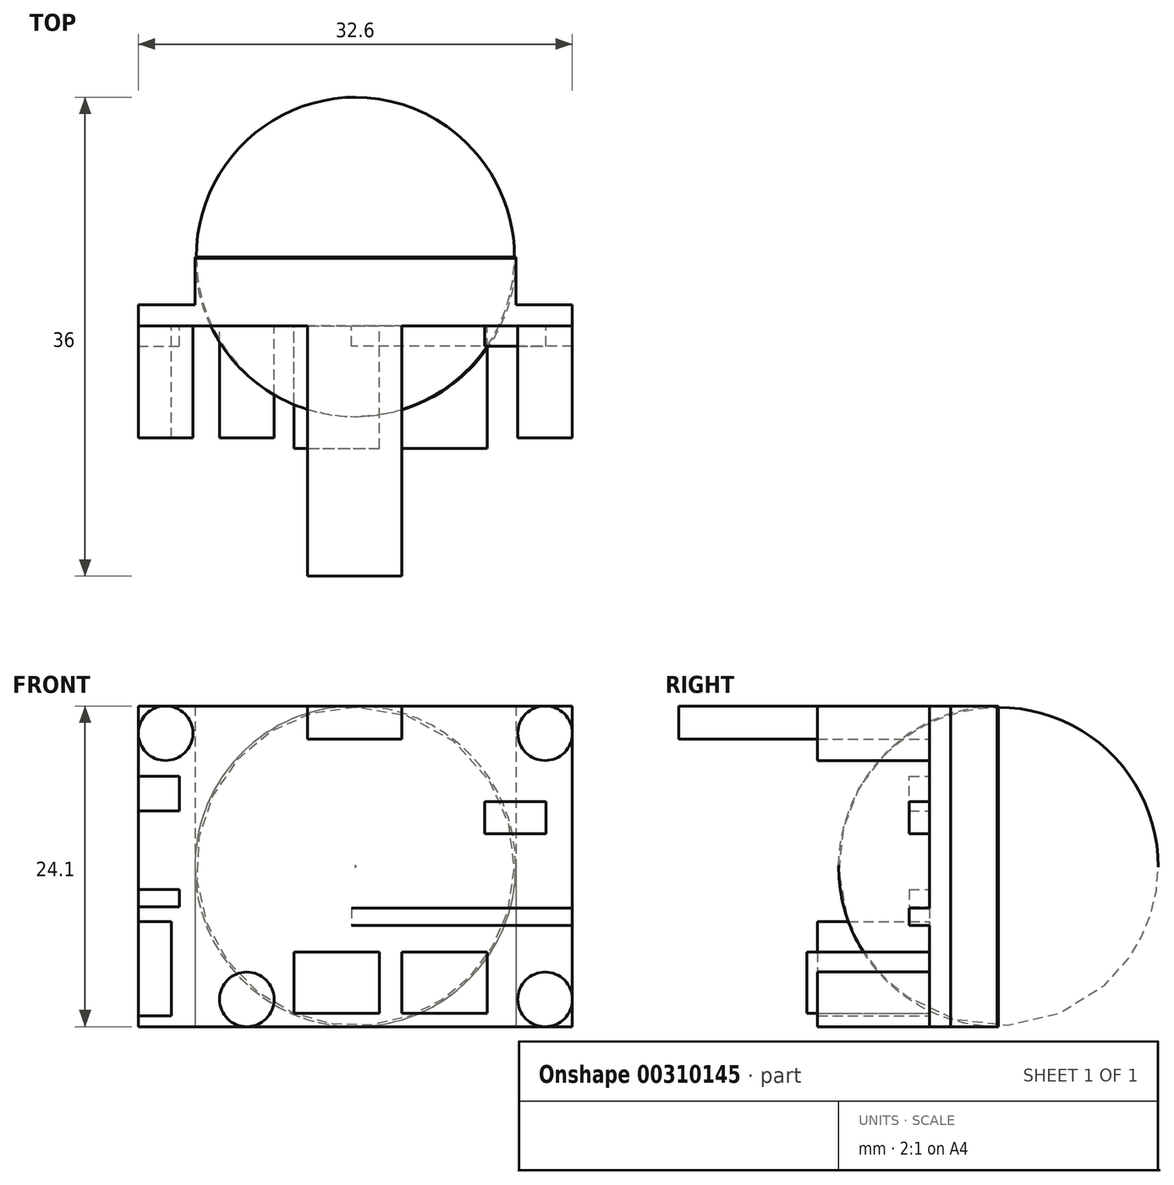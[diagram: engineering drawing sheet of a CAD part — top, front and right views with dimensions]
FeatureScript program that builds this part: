
annotation { "Feature Type Name" : "Feature", "Feature Type Description" : "" }
export const myFeature = defineFeature(function(context is Context, id is Id, definition is map)
    precondition{}
    {
        {
            var Q0;
            Q0=qCreatedBy(makeId("Front.planeOp"),FACE);
            var sketch = newSketch(context, id + "F0", { "sketchPlane" : qUnion([Q0])});
            skLineSegment(sketch, "E0.bottom", {"start": v(16.3, 12.05) * mm, "end": v(-16.3, 12.05) * mm});
            skLineSegment(sketch, "E0.top", {"start": v(16.3, -12.05) * mm, "end": v(-16.3, -12.05) * mm});
            skLineSegment(sketch, "E0.left", {"start": v(16.3, 12.05) * mm, "end": v(16.3, -12.05) * mm});
            skLineSegment(sketch, "E0.right", {"start": v(-16.3, 12.05) * mm, "end": v(-16.3, -12.05) * mm});
            skPoint(sketch, "E0.middle", {"position": v(0, 0) * mm});
            skLineSegment(sketch, "E1.bottom", {"start": v(12.05, 12.05) * mm, "end": v(-12.05, 12.05) * mm});
            skLineSegment(sketch, "E1.top", {"start": v(12.05, -12.05) * mm, "end": v(-12.05, -12.05) * mm});
            skLineSegment(sketch, "E1.left", {"start": v(12.05, 12.05) * mm, "end": v(12.05, -12.05) * mm});
            skLineSegment(sketch, "E1.right", {"start": v(-12.05, 12.05) * mm, "end": v(-12.05, -12.05) * mm});
            skCircle(sketch, "E2", {"center": v(0, 0) * mm, "radius": 12.05 * mm});
            skSolve(sketch);
        }
        {
            var Q0;
            Q0=qCreatedBy(makeId("Front.planeOp"),FACE);
            var sketch = newSketch(context, id + "F1", { "sketchPlane" : qUnion([Q0])});
            skCircle(sketch, "E3", {"center": v(-14.25, 10) * mm, "radius": 2.05 * mm});
            skCircle(sketch, "E4", {"center": v(14.25, 10) * mm, "radius": 2.05 * mm});
            skCircle(sketch, "E5", {"center": v(14.25, -10) * mm, "radius": 2.05 * mm});
            skCircle(sketch, "E6", {"center": v(-8.15, -10) * mm, "radius": 2.05 * mm});
            skLineSegment(sketch, "E7.bottom", {"start": v(-4.6, -6.45) * mm, "end": v(1.8, -6.45) * mm});
            skLineSegment(sketch, "E7.top", {"start": v(-4.6, -11.05) * mm, "end": v(1.8, -11.05) * mm});
            skLineSegment(sketch, "E7.left", {"start": v(-4.6, -6.45) * mm, "end": v(-4.6, -11.05) * mm});
            skLineSegment(sketch, "E7.right", {"start": v(1.8, -6.45) * mm, "end": v(1.8, -11.05) * mm});
            skLineSegment(sketch, "E8.bottom", {"start": v(3.5, -6.45) * mm, "end": v(9.9, -6.45) * mm});
            skLineSegment(sketch, "E8.top", {"start": v(3.5, -11.05) * mm, "end": v(9.9, -11.05) * mm});
            skLineSegment(sketch, "E8.left", {"start": v(3.5, -6.45) * mm, "end": v(3.5, -11.05) * mm});
            skLineSegment(sketch, "E8.right", {"start": v(9.9, -6.45) * mm, "end": v(9.9, -11.05) * mm});
            skLineSegment(sketch, "E9.bottom", {"start": v(-16.3, -4.15) * mm, "end": v(-13.8, -4.15) * mm});
            skLineSegment(sketch, "E9.top", {"start": v(-16.3, -11.25) * mm, "end": v(-13.8, -11.25) * mm});
            skLineSegment(sketch, "E9.left", {"start": v(-16.3, -4.15) * mm, "end": v(-16.3, -11.25) * mm});
            skLineSegment(sketch, "E9.right", {"start": v(-13.8, -4.15) * mm, "end": v(-13.8, -11.25) * mm});
            skLineSegment(sketch, "E10", {"start": v(-6.1, -8.53) * mm, "end": v(-6.1, -11.33) * mm, "construction": true});
            skLineSegment(sketch, "E11.bottom", {"start": v(-3.6, 9.55) * mm, "end": v(3.5, 9.55) * mm});
            skLineSegment(sketch, "E11.top", {"start": v(-3.6, 12.05) * mm, "end": v(3.5, 12.05) * mm});
            skLineSegment(sketch, "E11.left", {"start": v(-3.6, 9.55) * mm, "end": v(-3.6, 12.05) * mm});
            skLineSegment(sketch, "E11.right", {"start": v(3.5, 9.55) * mm, "end": v(3.5, 12.05) * mm});
            skLineSegment(sketch, "E12", {"start": v(12.2, -9.52) * mm, "end": v(12.2, -11.22) * mm, "construction": true});
            skLineSegment(sketch, "E13.bottom", {"start": v(9.7, 4.85) * mm, "end": v(14.3, 4.85) * mm});
            skLineSegment(sketch, "E13.top", {"start": v(9.7, 2.45) * mm, "end": v(14.3, 2.45) * mm});
            skLineSegment(sketch, "E13.left", {"start": v(9.7, 4.85) * mm, "end": v(9.7, 2.45) * mm});
            skLineSegment(sketch, "E13.right", {"start": v(14.3, 4.85) * mm, "end": v(14.3, 2.45) * mm});
            skLineSegment(sketch, "E14.bottom", {"start": v(16.3, -3.15) * mm, "end": v(-0.3, -3.15) * mm});
            skLineSegment(sketch, "E14.top", {"start": v(16.3, -4.45) * mm, "end": v(-0.3, -4.45) * mm});
            skLineSegment(sketch, "E14.left", {"start": v(16.3, -3.15) * mm, "end": v(16.3, -4.45) * mm});
            skLineSegment(sketch, "E14.right", {"start": v(-0.3, -3.15) * mm, "end": v(-0.3, -4.45) * mm});
            skLineSegment(sketch, "E15.bottom", {"start": v(-16.3, 4.15) * mm, "end": v(-13.2, 4.15) * mm});
            skLineSegment(sketch, "E15.top", {"start": v(-16.3, 6.75) * mm, "end": v(-13.2, 6.75) * mm});
            skLineSegment(sketch, "E15.left", {"start": v(-16.3, 4.15) * mm, "end": v(-16.3, 6.75) * mm});
            skLineSegment(sketch, "E15.right", {"start": v(-13.2, 4.15) * mm, "end": v(-13.2, 6.75) * mm});
            skLineSegment(sketch, "E16.bottom", {"start": v(-16.3, -1.75) * mm, "end": v(-13.2, -1.75) * mm});
            skLineSegment(sketch, "E16.top", {"start": v(-16.3, -3.05) * mm, "end": v(-13.2, -3.05) * mm});
            skLineSegment(sketch, "E16.left", {"start": v(-16.3, -1.75) * mm, "end": v(-16.3, -3.05) * mm});
            skLineSegment(sketch, "E16.right", {"start": v(-13.2, -1.75) * mm, "end": v(-13.2, -3.05) * mm});
            skSolve(sketch);
        }
        {
            var Q0;
            Q0 = qSketchRegion(id + "F0", true);
            extrude(context, id + "F2", {"entities" : qUnion([Q0]), "oppositeDirection" : true, "depth" : 1.6 * mm});
        }
        {
            var Q0;
            {var subQ1=sQuery(id+"F0.wireOp",EDGE,"E1.top");var subQ3=sQuery(id+"F0.wireOp",EDGE,"E2");var subQ4=makeQuery(id+"F0.imprint","INTERSECT",VERTEX,{"derivedFrom":[subQ1,subQ3]});Q0=makeQuery(id+"F0.imprint","IMPRINT",FACE,{"disambiguationData":[TD([[makeQuery(id+"F0.imprint","IMPRINT",EDGE,{"disambiguationData":[TD([[subQ4,1.0]])],"derivedFrom":subQ3}),-1.0]])]});}
            var Q1;
            {var subQ1=sQuery(id+"F0.wireOp",EDGE,"E1.bottom");var subQ3=sQuery(id+"F0.wireOp",EDGE,"E2");var subQ4=makeQuery(id+"F0.imprint","INTERSECT",VERTEX,{"derivedFrom":[subQ1,subQ3]});Q1=makeQuery(id+"F0.imprint","IMPRINT",FACE,{"disambiguationData":[TD([[makeQuery(id+"F0.imprint","IMPRINT",EDGE,{"disambiguationData":[TD([[subQ4,-1.0]])],"derivedFrom":subQ3}),-1.0]])]});}
            var Q2;
            {var subQ0=sQuery(id+"F0.wireOp",EDGE,"E2");var subQ1=makeQuery(id+"F0.imprint","INTERSECT",VERTEX,{"derivedFrom":[sQuery(id+"F0.wireOp",EDGE,"E1.bottom"),subQ0]});Q2=makeQuery(id+"F0.imprint","IMPRINT",FACE,{"disambiguationData":[TD([[makeQuery(id+"F0.imprint","IMPRINT",EDGE,{"disambiguationData":[TD([[subQ1,1.0]])],"derivedFrom":subQ0}),1.0]])]});}
            var Q3;
            {var subQ1=sQuery(id+"F0.wireOp",EDGE,"E1.bottom");var subQ3=sQuery(id+"F0.wireOp",EDGE,"E2");var subQ4=makeQuery(id+"F0.imprint","INTERSECT",VERTEX,{"derivedFrom":[subQ1,subQ3]});Q3=makeQuery(id+"F0.imprint","IMPRINT",FACE,{"disambiguationData":[TD([[makeQuery(id+"F0.imprint","IMPRINT",EDGE,{"disambiguationData":[TD([[subQ4,1.0]])],"derivedFrom":subQ3}),-1.0]])]});}
            var Q4;
            {var subQ1=sQuery(id+"F0.wireOp",EDGE,"E1.top");var subQ3=sQuery(id+"F0.wireOp",EDGE,"E2");var subQ4=makeQuery(id+"F0.imprint","INTERSECT",VERTEX,{"derivedFrom":[subQ1,subQ3]});Q4=makeQuery(id+"F0.imprint","IMPRINT",FACE,{"disambiguationData":[TD([[makeQuery(id+"F0.imprint","IMPRINT",EDGE,{"disambiguationData":[TD([[subQ4,-1.0]])],"derivedFrom":subQ3}),-1.0]])]});}
            extrude(context, id + "F3", {"entities" : qUnion([Q0, Q1, Q2, Q3, Q4]), "operationType" : NewBodyOperationType.ADD, "oppositeDirection" : true, "depth" : 5.1 * mm});
        }
        {
            var Q0;
            {var subQ0=sQuery(id+"F0.wireOp",EDGE,"E2");var subQ1=makeQuery(id+"F0.imprint","INTERSECT",VERTEX,{"derivedFrom":[sQuery(id+"F0.wireOp",EDGE,"E1.bottom"),subQ0]});Q0=makeQuery(id+"F0.imprint","IMPRINT",FACE,{"disambiguationData":[TD([[makeQuery(id+"F0.imprint","IMPRINT",EDGE,{"disambiguationData":[TD([[subQ1,1.0]])],"derivedFrom":subQ0}),1.0]])]});}
            extrude(context, id + "F4", {"entities" : qUnion([Q0]), "operationType" : NewBodyOperationType.ADD, "oppositeDirection" : true, "depth" : 17.2 * mm});
        }
        {
            var Q0;
            Q0=makeQuery(id+"F4.opExtrude","CAP_EDGE",EDGE,{"disambiguationData":[OSD([sQuery(id+"F0.wireOp",EDGE,"E2")])],"isStart":false});
            fillet(context, id + "F5", {"entities" : qUnion([Q0]), "radius" : 12 * mm, "tangentPropagation" : true, "allowEdgeOverflow" : false});
        }
        {
            var Q0;
            Q0=makeQuery(id+"F1.imprint","IMPRINT",FACE,{"disambiguationData":[TD([[makeQuery(id+"F1.imprint","IMPRINT",EDGE,{"derivedFrom":sQuery(id+"F1.wireOp",EDGE,"E3")}),1.0]])]});
            var Q1;
            Q1=makeQuery(id+"F1.imprint","IMPRINT",FACE,{"disambiguationData":[TD([[makeQuery(id+"F1.imprint","IMPRINT",EDGE,{"derivedFrom":sQuery(id+"F1.wireOp",EDGE,"E4")}),1.0]])]});
            var Q2;
            Q2=makeQuery(id+"F1.imprint","IMPRINT",FACE,{"disambiguationData":[TD([[makeQuery(id+"F1.imprint","IMPRINT",EDGE,{"derivedFrom":sQuery(id+"F1.wireOp",EDGE,"E5")}),1.0]])]});
            var Q3;
            Q3=makeQuery(id+"F1.imprint","IMPRINT",FACE,{"disambiguationData":[TD([[makeQuery(id+"F1.imprint","IMPRINT",EDGE,{"derivedFrom":sQuery(id+"F1.wireOp",EDGE,"E6")}),1.0]])]});
            var Q4;
            Q4=makeQuery(id+"F1.imprint","IMPRINT",FACE,{"disambiguationData":[TD([[makeQuery(id+"F1.imprint","IMPRINT",EDGE,{"derivedFrom":sQuery(id+"F1.wireOp",EDGE,"E9.bottom")}),-1.0]])]});
            var Q5;
            Q5=makeQuery(id+"F1.imprint","IMPRINT",FACE,{"disambiguationData":[TD([[makeQuery(id+"F1.imprint","IMPRINT",EDGE,{"derivedFrom":sQuery(id+"F1.wireOp",EDGE,"E11.bottom")}),1.0]])]});
            extrude(context, id + "F6", {"entities" : qUnion([Q0, Q1, Q2, Q3, Q4, Q5]), "operationType" : NewBodyOperationType.ADD, "depth" : 8.4 * mm});
        }
        {
            var Q0;
            Q0=makeQuery(id+"F1.imprint","IMPRINT",FACE,{"disambiguationData":[TD([[makeQuery(id+"F1.imprint","IMPRINT",EDGE,{"derivedFrom":sQuery(id+"F1.wireOp",EDGE,"E7.bottom")}),-1.0]])]});
            var Q1;
            Q1=makeQuery(id+"F1.imprint","IMPRINT",FACE,{"disambiguationData":[TD([[makeQuery(id+"F1.imprint","IMPRINT",EDGE,{"derivedFrom":sQuery(id+"F1.wireOp",EDGE,"E8.bottom")}),-1.0]])]});
            extrude(context, id + "F7", {"entities" : qUnion([Q0, Q1]), "operationType" : NewBodyOperationType.ADD, "depth" : 9.2 * mm});
        }
        {
            var Q0;
            Q0=makeQuery(id+"F1.imprint","IMPRINT",FACE,{"disambiguationData":[TD([[makeQuery(id+"F1.imprint","IMPRINT",EDGE,{"derivedFrom":sQuery(id+"F1.wireOp",EDGE,"E11.bottom")}),1.0]])]});
            extrude(context, id + "F8", {"entities" : qUnion([Q0]), "operationType" : NewBodyOperationType.ADD, "depth" : 18.8 * mm});
        }
        {
            var Q0;
            Q0=makeQuery(id+"F1.imprint","IMPRINT",FACE,{"disambiguationData":[TD([[makeQuery(id+"F1.imprint","IMPRINT",EDGE,{"derivedFrom":sQuery(id+"F1.wireOp",EDGE,"E16.bottom")}),-1.0]])]});
            var Q1;
            Q1=makeQuery(id+"F1.imprint","IMPRINT",FACE,{"disambiguationData":[TD([[makeQuery(id+"F1.imprint","IMPRINT",EDGE,{"derivedFrom":sQuery(id+"F1.wireOp",EDGE,"E13.bottom")}),-1.0]])]});
            var Q2;
            Q2=makeQuery(id+"F1.imprint","IMPRINT",FACE,{"disambiguationData":[TD([[makeQuery(id+"F1.imprint","IMPRINT",EDGE,{"derivedFrom":sQuery(id+"F1.wireOp",EDGE,"E14.bottom")}),1.0]])]});
            var Q3;
            Q3=makeQuery(id+"F1.imprint","IMPRINT",FACE,{"disambiguationData":[TD([[makeQuery(id+"F1.imprint","IMPRINT",EDGE,{"derivedFrom":sQuery(id+"F1.wireOp",EDGE,"E15.bottom")}),1.0]])]});
            extrude(context, id + "F9", {"entities" : qUnion([Q0, Q1, Q2, Q3]), "operationType" : NewBodyOperationType.ADD, "depth" : 1.5 * mm});
        }
    });
